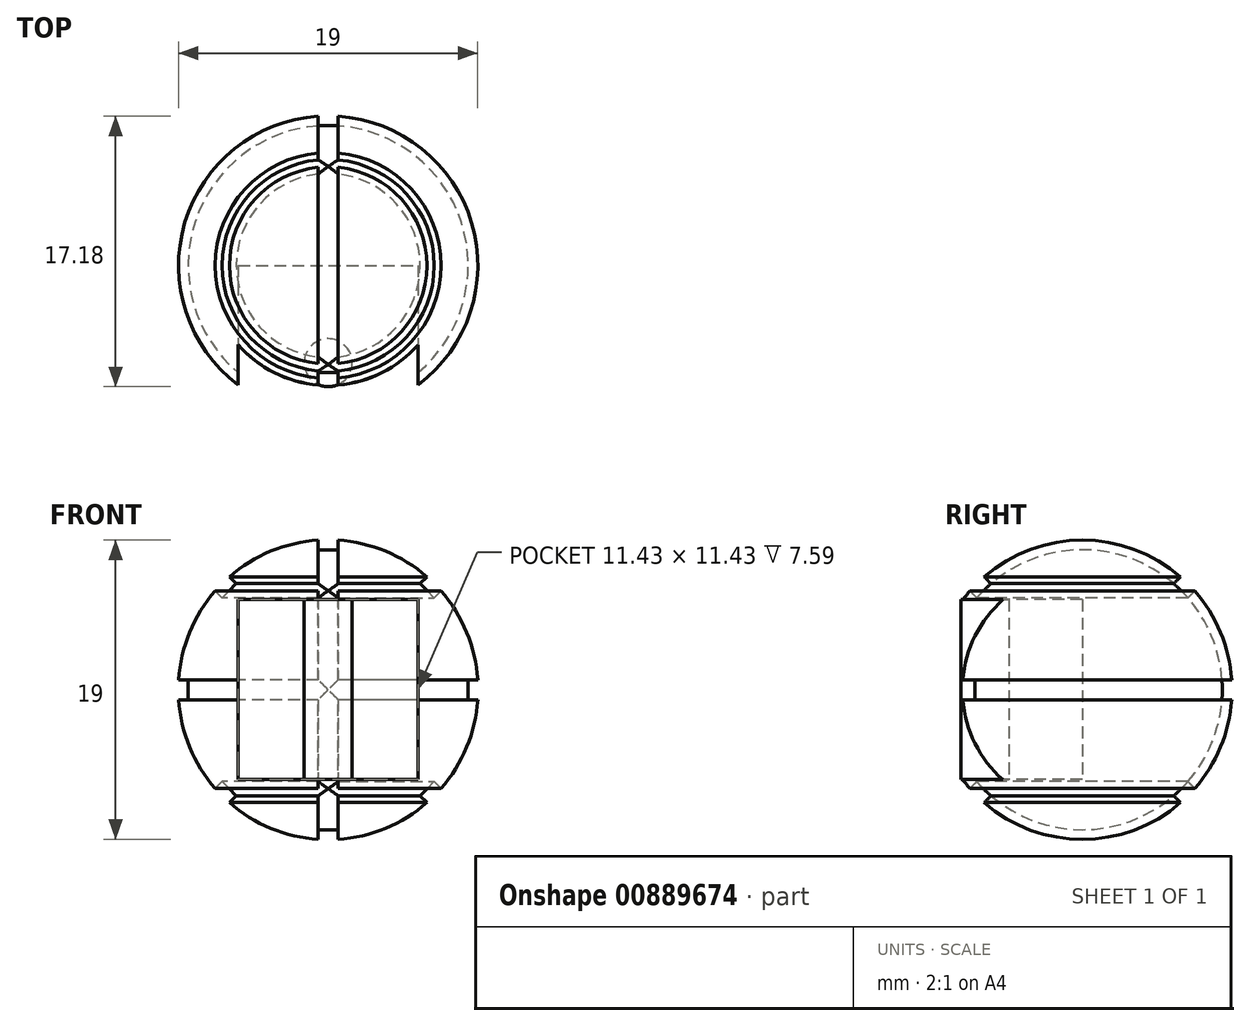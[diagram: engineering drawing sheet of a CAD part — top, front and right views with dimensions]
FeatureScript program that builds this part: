
annotation { "Feature Type Name" : "Feature", "Feature Type Description" : "" }
export const myFeature = defineFeature(function(context is Context, id is Id, definition is map)
    precondition{}
    {
        {
            var Q0;
            Q0=qCreatedBy(makeId("Front.planeOp"),FACE);
            var sketch = newSketch(context, id + "F0", { "sketchPlane" : qUnion([Q0])});
            skLineSegment(sketch, "E0", {"start": v(0, -9.53) * mm, "end": v(0, 9.53) * mm});
            skArc(sketch, "E1", {"start": v(0, -9.53) * mm, "mid": v(9.53, 0) * mm, "end": v(0, 9.53) * mm});
            skSolve(sketch);
        }
        {
            var Q0;
            Q0=makeQuery(id+"F0.imprint","IMPRINT",FACE,{"disambiguationData":[TD([[makeQuery(id+"F0.imprint","IMPRINT",EDGE,{"derivedFrom":sQuery(id+"F0.wireOp",EDGE,"E0")}),-1.0]])]});
            var Q1;
            Q1=sQuery(id+"F0.wireOp",EDGE,"E1");
            var Q2;
            Q2=sQuery(id+"F0.wireOp",EDGE,"E0");
            var Q3;
            Q3=sQuery(id+"F0.wireOp",EDGE,"E0");
            revolve(context, id + "F1", {"surfaceOperationType" : NewSurfaceOperationType.NEW, "entities" : qUnion([Q0]), "surfaceEntities" : qUnion([Q1, Q2]), "axis" : qUnion([Q3]), "revolveType" : RevolveType.FULL});
        }
        {
            var Q0;
            Q0=qCreatedBy(makeId("Front.planeOp"),FACE);
            var sketch = newSketch(context, id + "F2", { "sketchPlane" : qUnion([Q0])});
            skLineSegment(sketch, "E2.bottom", {"start": v(8.9, 0.64) * mm, "end": v(10.54, 0.64) * mm});
            skLineSegment(sketch, "E2.top", {"start": v(8.9, -0.64) * mm, "end": v(10.54, -0.64) * mm});
            skLineSegment(sketch, "E2.left", {"start": v(8.9, 0.64) * mm, "end": v(8.9, -0.64) * mm});
            skLineSegment(sketch, "E2.right", {"start": v(10.54, 0.64) * mm, "end": v(10.54, -0.64) * mm});
            skLineSegment(sketch, "E3", {"start": v(0, 0) * mm, "end": v(8.9, 0) * mm, "construction": true});
            skLineSegment(sketch, "E4", {"start": v(0, 0) * mm, "end": v(0, 3.4) * mm, "construction": true});
            skLineSegment(sketch, "E5", {"start": v(0, 0) * mm, "end": v(6.29, 6.29) * mm, "construction": true});
            skLineSegment(sketch, "E6", {"start": v(6.29, 6.29) * mm, "end": v(5.84, 6.74) * mm});
            skLineSegment(sketch, "E7", {"start": v(5.84, 6.74) * mm, "end": v(6.29, 7.18) * mm});
            skLineSegment(sketch, "E8", {"start": v(6.29, 7.18) * mm, "end": v(7.18, 6.29) * mm});
            skLineSegment(sketch, "E9", {"start": v(7.18, 6.29) * mm, "end": v(6.74, 5.84) * mm});
            skLineSegment(sketch, "E10", {"start": v(6.74, 5.84) * mm, "end": v(6.29, 6.29) * mm});
            skLineSegment(sketch, "E11.MirrorCS", {"start": v(6.74, -5.84) * mm, "end": v(6.29, -6.29) * mm});
            skLineSegment(sketch, "E12.MirrorCS", {"start": v(6.29, -7.18) * mm, "end": v(7.18, -6.29) * mm});
            skLineSegment(sketch, "E13.MirrorCS", {"start": v(5.84, -6.74) * mm, "end": v(6.29, -7.18) * mm});
            skLineSegment(sketch, "E14.MirrorCS", {"start": v(7.18, -6.29) * mm, "end": v(6.74, -5.84) * mm});
            skLineSegment(sketch, "E15.MirrorCS", {"start": v(6.29, -6.29) * mm, "end": v(5.84, -6.74) * mm});
            skSolve(sketch);
        }
        {
            var Q0;
            Q0 = qSketchRegion(id + "F2", true);
            var Q1;
            Q1=sQuery(id+"F2.wireOp",EDGE,"E4");
            revolve(context, id + "F3", {"operationType" : NewBodyOperationType.REMOVE, "surfaceOperationType" : NewSurfaceOperationType.NEW, "entities" : qUnion([Q0]), "axis" : qUnion([Q1]), "revolveType" : RevolveType.FULL, "oppositeDirection" : true});
        }
        {
            var Q0;
            Q0=qCreatedBy(makeId("Front.planeOp"),FACE);
            var sketch = newSketch(context, id + "F4", { "sketchPlane" : qUnion([Q0])});
            skLineSegment(sketch, "E16.bottom", {"start": v(-0.64, 9.86) * mm, "end": v(0.64, 9.86) * mm});
            skLineSegment(sketch, "E16.top", {"start": v(-0.64, 8.9) * mm, "end": v(0.64, 8.9) * mm});
            skLineSegment(sketch, "E16.left", {"start": v(-0.64, 9.86) * mm, "end": v(-0.64, 8.9) * mm});
            skLineSegment(sketch, "E16.right", {"start": v(0.63, 9.86) * mm, "end": v(0.63, 8.9) * mm});
            skLineSegment(sketch, "E17", {"start": v(0, 0) * mm, "end": v(0, 8.9) * mm, "construction": true});
            skLineSegment(sketch, "E18", {"start": v(0, 0) * mm, "end": v(-2.43, 0) * mm, "construction": true});
            skSolve(sketch);
        }
        {
            var Q0;
            Q0 = qSketchRegion(id + "F4", true);
            var Q1;
            Q1=sQuery(id+"F4.wireOp",EDGE,"E18");
            revolve(context, id + "F5", {"operationType" : NewBodyOperationType.REMOVE, "surfaceOperationType" : NewSurfaceOperationType.NEW, "entities" : qUnion([Q0]), "axis" : qUnion([Q1]), "revolveType" : RevolveType.FULL, "oppositeDirection" : true});
        }
        {
            var Q0;
            Q0=qCreatedBy(makeId("Front.planeOp"),FACE);
            cPlane(context, id + "F6", {"entities" : qUnion([Q0]), "cplaneType" : CPlaneType.OFFSET, "offset" : 9.52 * mm, "width" : 152.4 * mm, "height" : 152.4 * mm});
        }
        {
            var Q0;
            Q0=qCreatedBy(id+"F6.planeOp",FACE);
            var sketch = newSketch(context, id + "F7", { "sketchPlane" : qUnion([Q0])});
            skLineSegment(sketch, "E19.bottom", {"start": v(-5.72, 5.72) * mm, "end": v(5.7, 5.72) * mm});
            skLineSegment(sketch, "E19.top", {"start": v(-5.72, -5.7) * mm, "end": v(5.7, -5.7) * mm});
            skLineSegment(sketch, "E19.left", {"start": v(-5.72, 5.72) * mm, "end": v(-5.72, -5.7) * mm});
            skLineSegment(sketch, "E19.right", {"start": v(5.7, 5.72) * mm, "end": v(5.7, -5.7) * mm});
            skLineSegment(sketch, "E20", {"start": v(-5.72, 5.72) * mm, "end": v(5.7, -5.7) * mm, "construction": true});
            skSolve(sketch);
        }
        {
            var Q0;
            Q0 = qSketchRegion(id + "F7", true);
            extrude(context, id + "F8", {"entities" : qUnion([Q0]), "operationType" : NewBodyOperationType.REMOVE, "oppositeDirection" : true, "depth" : 9.52 * mm, "offsetDistance" : 25.4 * mm});
        }
        {
            var Q0;
            Q0=makeQuery(id+"F8.boolean.opBoolean","COPY",FACE,{"derivedFrom":makeQuery(id+"F8.opExtrude","SWEPT_FACE",FACE,{"disambiguationData":[OSD([sQuery(id+"F7.wireOp",EDGE,"E19.top")])]})});
            var sketch = newSketch(context, id + "F9", { "sketchPlane" : qUnion([Q0])});
            skCircle(sketch, "E21", {"center": v(0, -6.18) * mm, "radius": 1.52 * mm});
            skPoint(sketch, "E21.centerSnap0", {"position": v(0, -6.81) * mm});
            skLineSegment(sketch, "E22", {"start": v(0, -6.81) * mm, "end": v(0, -6.18) * mm, "construction": true});
            skSolve(sketch);
        }
        {
            var Q0;
            Q0 = qSketchRegion(id + "F9", true);
            var Q1;
            Q1=makeQuery(id+"F8.boolean.opBoolean","COPY",FACE,{"derivedFrom":makeQuery(id+"F8.opExtrude","SWEPT_FACE",FACE,{"disambiguationData":[OSD([sQuery(id+"F7.wireOp",EDGE,"E19.bottom")])]})});
            extrude(context, id + "F10", {"entities" : qUnion([Q0]), "operationType" : NewBodyOperationType.ADD, "endBound" : BoundingType.UP_TO_SURFACE, "depth" : 25.4 * mm, "endBoundEntityFace" : qUnion([Q1]), "offsetDistance" : 25.4 * mm});
        }
    });
